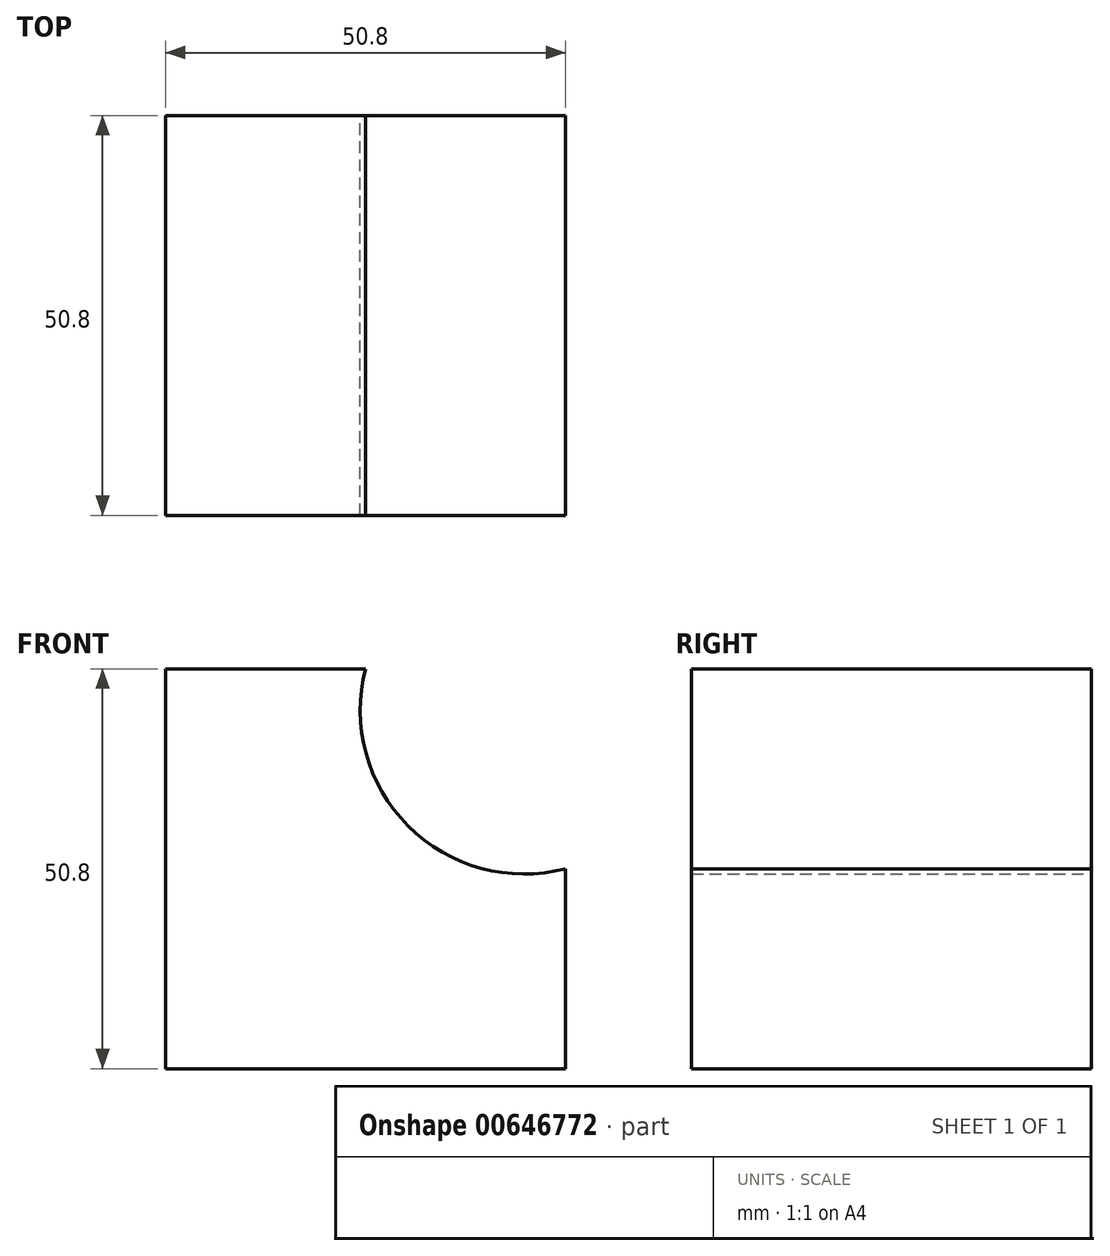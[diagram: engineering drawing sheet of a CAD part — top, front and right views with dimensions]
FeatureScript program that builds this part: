
annotation { "Feature Type Name" : "Feature", "Feature Type Description" : "" }
export const myFeature = defineFeature(function(context is Context, id is Id, definition is map)
    precondition{}
    {
        {
            var Q0;
            Q0=qCreatedBy(makeId("Front.planeOp"),FACE);
            var sketch = newSketch(context, id + "F0", { "sketchPlane" : qUnion([Q0])});
            skLineSegment(sketch, "E0", {"start": v(-19.95, 50.8) * mm, "end": v(-45.35, 50.8) * mm});
            skLineSegment(sketch, "E1", {"start": v(-45.35, 50.8) * mm, "end": v(-45.35, 0) * mm});
            skLineSegment(sketch, "E2", {"start": v(-45.35, 0) * mm, "end": v(5.45, 0) * mm});
            skLineSegment(sketch, "E3", {"start": v(5.45, 0) * mm, "end": v(5.45, 25.4) * mm});
            skArc(sketch, "E4", {"start": v(-19.95, 50.8) * mm, "mid": v(-14.53, 30.82) * mm, "end": v(5.45, 25.4) * mm});
            skSolve(sketch);
        }
        {
            var Q0;
            Q0=makeQuery(id+"F0.imprint","IMPRINT",FACE,{"disambiguationData":[TD([[makeQuery(id+"F0.imprint","IMPRINT",EDGE,{"derivedFrom":sQuery(id+"F0.wireOp",EDGE,"E0")}),1.0]])]});
            extrude(context, id + "F1", {"entities" : qUnion([Q0]), "depth" : 50.8 * mm, "offsetDistance" : 25.4 * mm});
        }
    });
